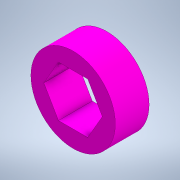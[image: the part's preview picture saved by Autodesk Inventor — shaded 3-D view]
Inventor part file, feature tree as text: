
AUTODESK INVENTOR PART (.ipt)
format: ipt  version: 2021.2 (Build 252289000, 289)  size: 110,080 bytes
history: native  units: in
note: dims shown in document units (in); Inventor stores cm internally (conversion verified against a paired STEP export)
features: extrude x1, sketch x1
ambient origin geometry x8: Origin, YZ Plane, XZ Plane, XY Plane, X Axis, Y Axis, Z Axis, Center Point
bodies: Solid1 (feature_tree)
feature tree (2):
  extrude  "Extrusion1"  Depth=0.25in
  sketch  "Sketch1"  dims[d0=0.375in d2=0.625in d3=0.096in d4=0.25in d5=0.0in]
